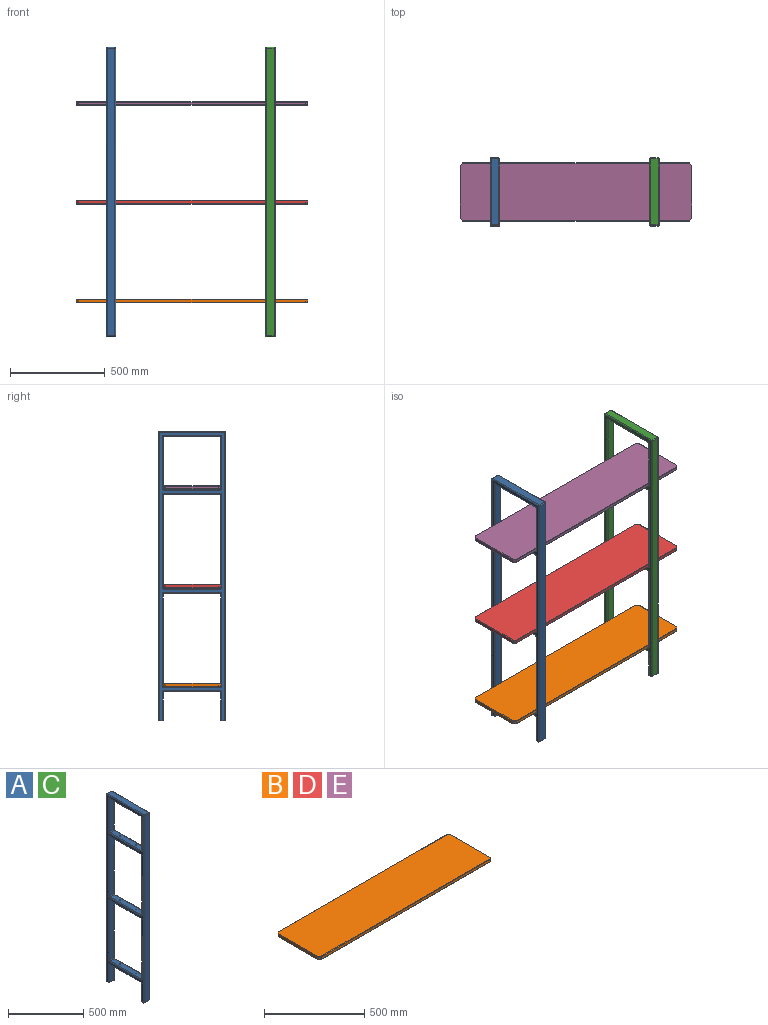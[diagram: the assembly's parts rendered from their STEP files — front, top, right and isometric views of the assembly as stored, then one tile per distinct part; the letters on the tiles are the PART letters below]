
ASSEMBLY  parts=5 mates=4
PART A: 114 faces, bbox 50.8x355.6x1524 mm
  f0: plane 269.11x40.64mm, normal (0,1,0), area 10936.6mm2, adj f85,f86,f89,f90
  f1: plane 294.64x40.64mm, normal (0,0,-1), area 11974.2mm2, adj f63,f67,f69,f86
  f2: plane 269.11x40.64mm, normal (0,-1,0), area 10936.6mm2, adj f61,f62,f66,f67
  f3: plane 484.37x40.64mm, normal (0,1,0), area 19684.8mm2, adj f93,f94,f97,f98
  f4: plane 294.64x40.64mm, normal (0,0,-1), area 11910.8mm2, adj f51,f55,f57,f94,f112,f113
  f5: plane 484.37x40.64mm, normal (0,-1,0), area 19684.8mm2, adj f49,f50,f54,f55
  f6: plane 294.64x40.64mm, normal (0,0,-1), area 11910.8mm2, adj f39,f43,f45,f102,f108,f109
  f7: plane 484.37x40.64mm, normal (0,-1,0), area 19684.8mm2, adj f37,f38,f42,f43
  f8: plane 294.64x40.64mm, normal (0,0,1), area 11910.8mm2, adj f34,f36,f37,f105,f112,f113
  f9: plane 50.8x20.32mm, normal (0,0,-1), area 1021.2mm2, adj f18,f20,f21,f22,f24,f83
  f10: plane 1513.84x40.64mm, normal (0,1,0), area 61522.5mm2, adj f77,f81,f82,f83
  f11: plane 345.44x40.64mm, normal (0,0,1), area 14038.7mm2, adj f72,f76,f77,f78
  f12: plane 1513.84x40.64mm, normal (0,-1,0), area 61522.5mm2, adj f70,f71,f72,f73
  f13: plane 50.8x20.32mm, normal (0,0,-1), area 1021.2mm2, adj f14,f20,f21,f27,f33,f70
  f14: plane 147.32x40.64mm, normal (0,1,0), area 5987.1mm2, adj f13,f27,f31,f33
  f15: plane 294.64x40.64mm, normal (0,0,-1), area 11910.8mm2, adj f25,f26,f30,f31,f110,f111
  f16: plane 294.64x40.64mm, normal (0,0,1), area 11910.8mm2, adj f46,f48,f49,f97,f110,f111
  f17: plane 484.37x40.64mm, normal (0,1,0), area 19684.8mm2, adj f101,f102,f105,f106
  f18: plane 147.32x40.64mm, normal (0,-1,0), area 5987.1mm2, adj f9,f22,f24,f25
  f19: plane 294.64x40.64mm, normal (0,0,1), area 11910.8mm2, adj f58,f60,f61,f89,f108,f109
  f20: plane 1518.92x345.44mm, normal (1,0,0), area 66332.9mm2, adj f9,f13,f24,f28,f30,f32,f33,f36
  f21: plane 1518.92x345.44mm, normal (-1,0,0), area 66332.9mm2, adj f9,f13,f22,f23,f26,f27,f29,f34
  f22: cylinder r=5.08mm len=147.32mm, axis (0,0,-1), area 1175.6mm2, adj f9,f18,f21,f23
  f23: torus R=10.16mm, axis (1,0,0), area 86.8mm2, adj f21,f22,f25,f26
  f24: cylinder r=5.08mm len=147.32mm, axis (0,0,1), area 1175.6mm2, adj f9,f18,f20,f28
  f25: cylinder r=5.08mm len=40.64mm, axis (1,0,0), area 324.3mm2, adj f15,f18,f23,f28
  f26: cylinder r=5.08mm len=294.64mm, axis (0,1,0), area 2351.1mm2, adj f15,f21,f23,f29
  f27: cylinder r=5.08mm len=147.32mm, axis (0,0,1), area 1175.6mm2, adj f13,f14,f21,f29
  f28: torus R=10.16mm, axis (1,0,0), area 86.8mm2, adj f20,f24,f25,f30
  f29: torus R=10.16mm, axis (1,0,0), area 86.8mm2, adj f21,f26,f27,f31
  f30: cylinder r=5.08mm len=294.64mm, axis (0,-1,0), area 2351.1mm2, adj f15,f20,f28,f32
  f31: cylinder r=5.08mm len=40.64mm, axis (-1,0,0), area 324.3mm2, adj f14,f15,f29,f32
  f32: torus R=10.16mm, axis (1,0,0), area 86.8mm2, adj f20,f30,f31,f33
  f33: cylinder r=5.08mm len=147.32mm, axis (0,0,-1), area 1175.6mm2, adj f13,f14,f20,f32
  f34: cylinder r=5.08mm len=294.64mm, axis (0,-1,0), area 2351.1mm2, adj f8,f21,f35,f107
  f35: torus R=10.16mm, axis (1,0,0), area 86.8mm2, adj f21,f34,f37,f38
  f36: cylinder r=5.08mm len=294.64mm, axis (0,1,0), area 2351.1mm2, adj f8,f20,f40,f103
  f37: cylinder r=5.08mm len=40.64mm, axis (-1,0,0), area 324.3mm2, adj f7,f8,f35,f40
  f38: cylinder r=5.08mm len=484.37mm, axis (0,0,-1), area 3865.1mm2, adj f7,f21,f35,f41
  f39: cylinder r=5.08mm len=294.64mm, axis (0,1,0), area 2351.1mm2, adj f6,f21,f41,f104
  f40: torus R=10.16mm, axis (1,0,0), area 86.8mm2, adj f20,f36,f37,f42
  f41: torus R=10.16mm, axis (1,0,0), area 86.8mm2, adj f21,f38,f39,f43
  f42: cylinder r=5.08mm len=484.37mm, axis (0,0,1), area 3865.1mm2, adj f7,f20,f40,f44
  f43: cylinder r=5.08mm len=40.64mm, axis (-1,0,0), area 324.3mm2, adj f6,f7,f41,f44
  f44: torus R=10.16mm, axis (1,0,0), area 86.8mm2, adj f20,f42,f43,f45
  f45: cylinder r=5.08mm len=294.64mm, axis (0,-1,0), area 2351.1mm2, adj f6,f20,f44,f100
  f46: cylinder r=5.08mm len=294.64mm, axis (0,-1,0), area 2351.1mm2, adj f16,f21,f47,f99
  f47: torus R=10.16mm, axis (1,0,0), area 86.8mm2, adj f21,f46,f49,f50
  f48: cylinder r=5.08mm len=294.64mm, axis (0,1,0), area 2351.1mm2, adj f16,f20,f52,f95
  f49: cylinder r=5.08mm len=40.64mm, axis (-1,0,0), area 324.3mm2, adj f5,f16,f47,f52
  f50: cylinder r=5.08mm len=484.37mm, axis (0,0,-1), area 3865.1mm2, adj f5,f21,f47,f53
  f51: cylinder r=5.08mm len=294.64mm, axis (0,1,0), area 2351.1mm2, adj f4,f21,f53,f96
  f52: torus R=10.16mm, axis (1,0,0), area 86.8mm2, adj f20,f48,f49,f54
  f53: torus R=10.16mm, axis (1,0,0), area 86.8mm2, adj f21,f50,f51,f55
  f54: cylinder r=5.08mm len=484.37mm, axis (0,0,1), area 3865.1mm2, adj f5,f20,f52,f56
  f55: cylinder r=5.08mm len=40.64mm, axis (1,0,0), area 324.3mm2, adj f4,f5,f53,f56
  f56: torus R=10.16mm, axis (1,0,0), area 86.8mm2, adj f20,f54,f55,f57
  f57: cylinder r=5.08mm len=294.64mm, axis (0,-1,0), area 2351.1mm2, adj f4,f20,f56,f92
  f58: cylinder r=5.08mm len=294.64mm, axis (0,-1,0), area 2351.1mm2, adj f19,f21,f59,f91
  f59: torus R=10.16mm, axis (1,0,0), area 86.8mm2, adj f21,f58,f61,f62
  f60: cylinder r=5.08mm len=294.64mm, axis (0,1,0), area 2351.1mm2, adj f19,f20,f64,f87
  f61: cylinder r=5.08mm len=40.64mm, axis (1,0,0), area 324.3mm2, adj f2,f19,f59,f64
  f62: cylinder r=5.08mm len=269.11mm, axis (0,0,-1), area 2147.4mm2, adj f2,f21,f59,f65
  f63: cylinder r=5.08mm len=294.64mm, axis (0,1,0), area 2351.1mm2, adj f1,f21,f65,f88
  f64: torus R=10.16mm, axis (1,0,0), area 86.8mm2, adj f20,f60,f61,f66
  f65: torus R=10.16mm, axis (1,0,0), area 86.8mm2, adj f21,f62,f63,f67
  f66: cylinder r=5.08mm len=269.11mm, axis (0,0,1), area 2147.4mm2, adj f2,f20,f64,f68
  f67: cylinder r=5.08mm len=40.64mm, axis (1,0,0), area 324.3mm2, adj f1,f2,f65,f68
  f68: torus R=10.16mm, axis (1,0,0), area 86.8mm2, adj f20,f66,f67,f69
  f69: cylinder r=5.08mm len=294.64mm, axis (0,-1,0), area 2351.1mm2, adj f1,f20,f68,f84
  f70: cylinder r=5.08mm len=50.8mm, axis (-1,0,0), area 375.9mm2, adj f12,f13,f71,f73
  f71: cylinder r=5.08mm len=1518.92mm, axis (0,0,1), area 12105.7mm2, adj f12,f20,f70,f74
  f72: cylinder r=5.08mm len=40.64mm, axis (-1,0,0), area 324.3mm2, adj f11,f12,f74,f75
  f73: cylinder r=5.08mm len=1518.92mm, axis (0,0,-1), area 12105.7mm2, adj f12,f21,f70,f75
  f74: sphere r=5.08mm, area 40.5mm2, adj f71,f72,f76
  f75: sphere r=5.08mm, area 40.5mm2, adj f72,f73,f78
  f76: cylinder r=5.08mm len=345.44mm, axis (0,1,0), area 2756.5mm2, adj f11,f20,f74,f79
  f77: cylinder r=5.08mm len=40.64mm, axis (1,0,0), area 324.3mm2, adj f10,f11,f79,f80
  f78: cylinder r=5.08mm len=345.44mm, axis (0,-1,0), area 2756.5mm2, adj f11,f21,f75,f80
  f79: sphere r=5.08mm, area 40.5mm2, adj f76,f77,f81
  f80: sphere r=5.08mm, area 40.5mm2, adj f77,f78,f82
  f81: cylinder r=5.08mm len=1518.92mm, axis (0,0,-1), area 12105.7mm2, adj f10,f20,f79,f83
  f82: cylinder r=5.08mm len=1518.92mm, axis (0,0,1), area 12105.7mm2, adj f10,f21,f80,f83
  f83: cylinder r=5.08mm len=50.8mm, axis (-1,0,0), area 375.9mm2, adj f9,f10,f81,f82
  f84: torus R=10.16mm, axis (1,0,0), area 86.8mm2, adj f20,f69,f85,f86
  f85: cylinder r=5.08mm len=269.11mm, axis (0,0,-1), area 2147.4mm2, adj f0,f20,f84,f87
  f86: cylinder r=5.08mm len=40.64mm, axis (-1,0,0), area 324.3mm2, adj f0,f1,f84,f88
  f87: torus R=10.16mm, axis (1,0,0), area 86.8mm2, adj f20,f60,f85,f89
  f88: torus R=10.16mm, axis (1,0,0), area 86.8mm2, adj f21,f63,f86,f90
  f89: cylinder r=5.08mm len=40.64mm, axis (-1,0,0), area 324.3mm2, adj f0,f19,f87,f91
  f90: cylinder r=5.08mm len=269.11mm, axis (0,0,1), area 2147.4mm2, adj f0,f21,f88,f91
  f91: torus R=10.16mm, axis (1,0,0), area 86.8mm2, adj f21,f58,f89,f90
  f92: torus R=10.16mm, axis (1,0,0), area 86.8mm2, adj f20,f57,f93,f94
  f93: cylinder r=5.08mm len=484.37mm, axis (0,0,-1), area 3865.1mm2, adj f3,f20,f92,f95
  f94: cylinder r=5.08mm len=40.64mm, axis (-1,0,0), area 324.3mm2, adj f3,f4,f92,f96
  f95: torus R=10.16mm, axis (1,0,0), area 86.8mm2, adj f20,f48,f93,f97
  f96: torus R=10.16mm, axis (1,0,0), area 86.8mm2, adj f21,f51,f94,f98
  f97: cylinder r=5.08mm len=40.64mm, axis (1,0,0), area 324.3mm2, adj f3,f16,f95,f99
  f98: cylinder r=5.08mm len=484.37mm, axis (0,0,1), area 3865.1mm2, adj f3,f21,f96,f99
  f99: torus R=10.16mm, axis (1,0,0), area 86.8mm2, adj f21,f46,f97,f98
  f100: torus R=10.16mm, axis (1,0,0), area 86.8mm2, adj f20,f45,f101,f102
  f101: cylinder r=5.08mm len=484.37mm, axis (0,0,-1), area 3865.1mm2, adj f17,f20,f100,f103
  f102: cylinder r=5.08mm len=40.64mm, axis (1,0,0), area 324.3mm2, adj f6,f17,f100,f104
  f103: torus R=10.16mm, axis (1,0,0), area 86.8mm2, adj f20,f36,f101,f105
  f104: torus R=10.16mm, axis (1,0,0), area 86.8mm2, adj f21,f39,f102,f106
  f105: cylinder r=5.08mm len=40.64mm, axis (1,0,0), area 324.3mm2, adj f8,f17,f103,f107
  f106: cylinder r=5.08mm len=484.37mm, axis (0,0,1), area 3865.1mm2, adj f17,f21,f104,f107
  f107: torus R=10.16mm, axis (1,0,0), area 86.8mm2, adj f21,f34,f105,f106
  f108: cylinder r=3.17mm len=26.94mm, axis (0,0,-1), area 537.4mm2, adj f6,f19
  f109: cylinder r=3.17mm len=26.94mm, axis (0,0,-1), area 537.4mm2, adj f6,f19
  f110: cylinder r=3.17mm len=25.4mm, axis (0,0,-1), area 506.7mm2, adj f15,f16
  f111: cylinder r=3.17mm len=25.4mm, axis (0,0,-1), area 506.7mm2, adj f15,f16
  f112: cylinder r=3.17mm len=25.4mm, axis (0,0,-1), area 506.7mm2, adj f4,f8
  f113: cylinder r=3.17mm len=25.4mm, axis (0,0,-1), area 506.7mm2, adj f4,f8
PART B: 50 faces, bbox 1219.2x304.8x19.1 mm
  f0: plane 13.97x11.21mm, normal (0.71,0.71,0), area 221.5mm2, adj f42,f45,f46,f49
  f1: plane 13.97x11.21mm, normal (0.71,-0.71,0), area 221.5mm2, adj f34,f37,f38,f41
  f2: plane 13.97x11.21mm, normal (-0.71,0.71,0), area 221.5mm2, adj f26,f29,f30,f33
  f3: plane 13.97x11.21mm, normal (-0.71,-0.71,0), area 221.5mm2, adj f18,f21,f22,f25
  f4: plane 1214.12x299.72mm, normal (0,0,1), area 363644.6mm2, adj f14,f15,f16,f17,f18,f26,f34,f42
  f5: plane 1214.12x299.72mm, normal (0,0,-1), area 363644.6mm2, adj f10,f11,f12,f13,f25,f33,f41,f49
  f6: plane 1191.7x13.97mm, normal (0,1,0), area 16648mm2, adj f10,f14,f30,f46
  f7: plane 277.3x13.97mm, normal (-1,0,0), area 3873.8mm2, adj f11,f15,f22,f29
  f8: plane 1191.7x13.97mm, normal (0,-1,0), area 16648mm2, adj f13,f17,f21,f37
  f9: plane 277.3x13.97mm, normal (1,0,0), area 3873.8mm2, adj f12,f16,f38,f45
  f10: cylinder r=2.54mm len=1191.7mm, axis (-1,0,0), area 4754.7mm2, adj f5,f6,f32,f48
  f11: cylinder r=2.54mm len=277.3mm, axis (0,-1,0), area 1106.4mm2, adj f5,f7,f24,f31
  f12: cylinder r=2.54mm len=277.3mm, axis (0,1,0), area 1106.4mm2, adj f5,f9,f40,f47
  f13: cylinder r=2.54mm len=1191.7mm, axis (1,0,0), area 4754.7mm2, adj f5,f8,f23,f39
  f14: cylinder r=2.54mm len=1191.7mm, axis (1,0,0), area 4754.7mm2, adj f4,f6,f28,f44
  f15: cylinder r=2.54mm len=277.3mm, axis (0,1,0), area 1106.4mm2, adj f4,f7,f20,f27
  f16: cylinder r=2.54mm len=277.3mm, axis (0,-1,0), area 1106.4mm2, adj f4,f9,f36,f43
  f17: cylinder r=2.54mm len=1191.7mm, axis (-1,0,0), area 4754.7mm2, adj f4,f8,f19,f35
  f18: cylinder r=2.54mm len=13.01mm, axis (0.71,-0.71,0), area 63.3mm2, adj f3,f4,f19,f20
  f19: sphere r=2.54mm, area 5.1mm2, adj f17,f18,f21
  f20: sphere r=2.54mm, area 5.1mm2, adj f15,f18,f22
  f21: cylinder r=2.54mm len=13.97mm, axis (0,0,-1), area 27.9mm2, adj f3,f8,f19,f23
  f22: cylinder r=2.54mm len=13.97mm, axis (0,0,1), area 27.9mm2, adj f3,f7,f20,f24
  f23: sphere r=2.54mm, area 5.1mm2, adj f13,f21,f25
  f24: sphere r=2.54mm, area 5.1mm2, adj f11,f22,f25
  f25: cylinder r=2.54mm len=13.01mm, axis (-0.71,0.71,0), area 63.3mm2, adj f3,f5,f23,f24
  f26: cylinder r=2.54mm len=13.01mm, axis (0.71,0.71,0), area 63.3mm2, adj f2,f4,f27,f28
  f27: sphere r=2.54mm, area 5.1mm2, adj f15,f26,f29
  f28: sphere r=2.54mm, area 5.1mm2, adj f14,f26,f30
  f29: cylinder r=2.54mm len=13.97mm, axis (0,0,1), area 27.9mm2, adj f2,f7,f27,f31
  f30: cylinder r=2.54mm len=13.97mm, axis (0,0,1), area 27.9mm2, adj f2,f6,f28,f32
  f31: sphere r=2.54mm, area 5.1mm2, adj f11,f29,f33
  f32: sphere r=2.54mm, area 5.1mm2, adj f10,f30,f33
  f33: cylinder r=2.54mm len=13.01mm, axis (-0.71,-0.71,0), area 63.3mm2, adj f2,f5,f31,f32
  f34: cylinder r=2.54mm len=13.01mm, axis (-0.71,-0.71,0), area 63.3mm2, adj f1,f4,f35,f36
  f35: sphere r=2.54mm, area 5.1mm2, adj f17,f34,f37
  f36: sphere r=2.54mm, area 5.1mm2, adj f16,f34,f38
  f37: cylinder r=2.54mm len=13.97mm, axis (0,0,-1), area 27.9mm2, adj f1,f8,f35,f39
  f38: cylinder r=2.54mm len=13.97mm, axis (0,0,-1), area 27.9mm2, adj f1,f9,f36,f40
  f39: sphere r=2.54mm, area 5.1mm2, adj f13,f37,f41
  f40: sphere r=2.54mm, area 5.1mm2, adj f12,f38,f41
  f41: cylinder r=2.54mm len=13.01mm, axis (-0.71,-0.71,0), area 63.3mm2, adj f1,f5,f39,f40
  f42: cylinder r=2.54mm len=13.01mm, axis (-0.71,0.71,0), area 63.3mm2, adj f0,f4,f43,f44
  f43: sphere r=2.54mm, area 5.1mm2, adj f16,f42,f45
  f44: sphere r=2.54mm, area 5.1mm2, adj f14,f42,f46
  f45: cylinder r=2.54mm len=13.97mm, axis (0,0,-1), area 27.9mm2, adj f0,f9,f43,f47
  f46: cylinder r=2.54mm len=13.97mm, axis (0,0,1), area 27.9mm2, adj f0,f6,f44,f48
  f47: sphere r=2.54mm, area 5.1mm2, adj f12,f45,f49
  f48: sphere r=2.54mm, area 5.1mm2, adj f10,f46,f49
  f49: cylinder r=2.54mm len=13.01mm, axis (-0.71,0.71,0), area 63.3mm2, adj f0,f5,f47,f48
PART C: same geometry as A
PART D: same geometry as B
PART E: same geometry as B
PLACE A t=(300.45,602,205.94)mm
PLACE B t=(752.37,730.19,290.02)mm
PLACE C t=(1139.17,602,205.94)mm
PLACE D t=(752.37,730.19,810.72)mm
PLACE E t=(752.37,730.19,1331.42)mm
MATE planar B.f5 <-> C.f16  axis (0,0,-1) through (752.37,730.19,290.02)mm
MATE planar B.f5 <-> A.f16  axis (0,0,-1) through (752.37,730.19,290.02)mm
MATE planar B.f6 <-> C.f5  axis (0,1,0) through (752.37,882.59,299.54)mm
MATE planar A.f5 <-> B.f6  axis (0,-1,0) through (325.85,882.59,537.28)mm
